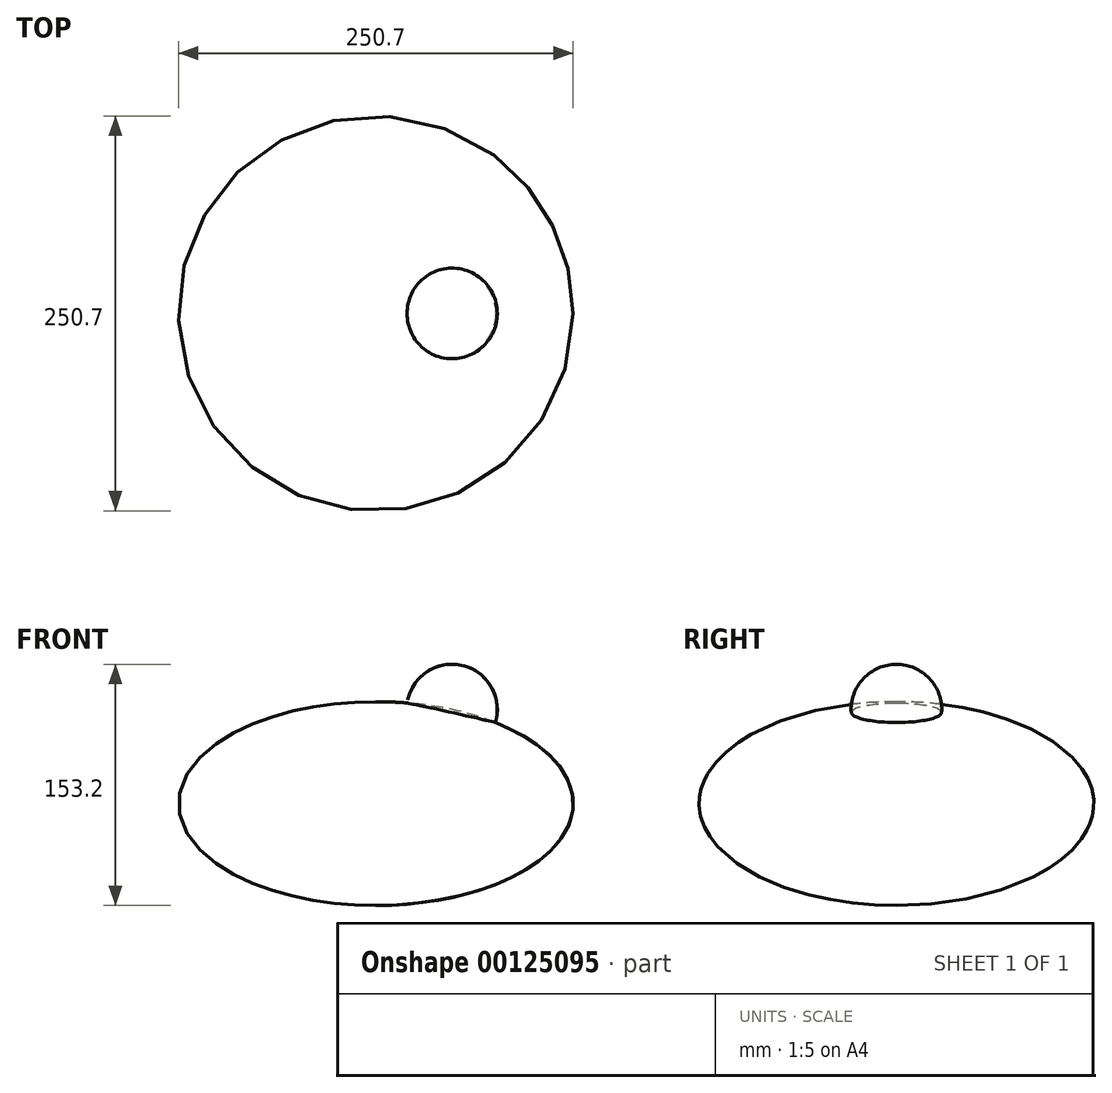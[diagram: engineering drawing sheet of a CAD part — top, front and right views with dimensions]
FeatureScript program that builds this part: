
annotation { "Feature Type Name" : "Feature", "Feature Type Description" : "" }
export const myFeature = defineFeature(function(context is Context, id is Id, definition is map)
    precondition{}
    {
        {
            var Q0;
            Q0=qCreatedBy(makeId("Front.planeOp"),FACE);
            var sketch = newSketch(context, id + "F0", { "sketchPlane" : qUnion([Q0])});
            skEllipse(sketch, "E0", {"center": v(0, 0) * mm, "majorRadius": 125.35 * mm, "minorRadius": 64.71 * mm, "majorAxis": v(1, 0)});
            skLineSegment(sketch, "E1", {"start": v(0, 0) * mm, "end": v(0, 116.2) * mm});
            skPoint(sketch, "E1.endSnap0", {"position": v(0, 64.71) * mm});
            skLineSegment(sketch, "E2", {"start": v(0, 0) * mm, "end": v(0, -64.71) * mm});
            skCircle(sketch, "E3", {"center": v(48.4, 59.7) * mm, "radius": 28.8 * mm});
            skLineSegment(sketch, "E4", {"start": v(48.4, 59.7) * mm, "end": v(93.17, 50.02) * mm});
            skLineSegment(sketch, "E5", {"start": v(48.4, 59.7) * mm, "end": v(21.95, 65.41) * mm});
            skLineSegment(sketch, "E6", {"start": v(21.95, 65.41) * mm, "end": v(16.54, 66.58) * mm});
            skSolve(sketch);
        }
        {
            var Q0;
            {var subQ0=sQuery(id+"F0.wireOp",EDGE,"E2");Q0=makeQuery(id+"F0.imprint","IMPRINT",FACE,{"disambiguationData":[TD([[makeQuery(id+"F0.imprint","IMPRINT",EDGE,{"derivedFrom":subQ0}),1.0]])]});}
            var Q1;
            {var subQ0=sQuery(id+"F0.wireOp",EDGE,"E0");var subQ2=sQuery(id+"F0.wireOp",EDGE,"E3");var subQ3=makeQuery(id+"F0.imprint","INTERSECT",VERTEX,{"disambiguationData":[OD(0.0)],"derivedFrom":[subQ0,subQ2]});Q1=makeQuery(id+"F0.imprint","IMPRINT",FACE,{"disambiguationData":[TD([[makeQuery(id+"F0.imprint","IMPRINT",EDGE,{"disambiguationData":[TD([[subQ3,1.0]])],"derivedFrom":subQ2}),1.0]])]});}
            var Q2;
            Q2=sQuery(id+"F0.wireOp",EDGE,"E1");
            revolve(context, id + "F1", {"entities" : qUnion([Q0, Q1]), "axis" : qUnion([Q2]), "revolveType" : RevolveType.FULL});
        }
        {
            var Q0;
            {var subQ5=sQuery(id+"F0.wireOp",EDGE,"E5");Q0=makeQuery(id+"F0.imprint","IMPRINT",FACE,{"disambiguationData":[TD([[makeQuery(id+"F0.imprint","IMPRINT",EDGE,{"derivedFrom":subQ5}),-1.0]])]});}
            var Q1;
            Q1=sQuery(id+"F0.wireOp",EDGE,"E4");
            revolve(context, id + "F2", {"operationType" : NewBodyOperationType.ADD, "entities" : qUnion([Q0]), "axis" : qUnion([Q1]), "revolveType" : RevolveType.FULL});
        }
    });
